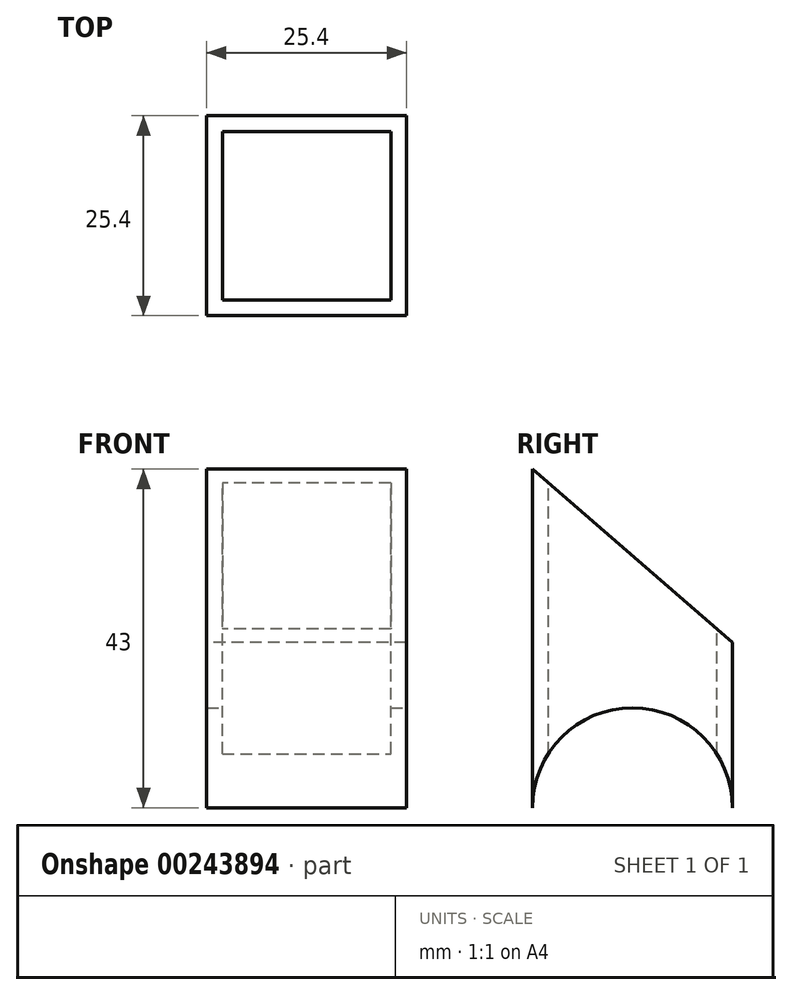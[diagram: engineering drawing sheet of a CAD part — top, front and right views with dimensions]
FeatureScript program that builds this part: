
annotation { "Feature Type Name" : "Feature", "Feature Type Description" : "" }
export const myFeature = defineFeature(function(context is Context, id is Id, definition is map)
    precondition{}
    {
        {
            var Q0;
            Q0=qCreatedBy(makeId("Right.planeOp"),FACE);
            var sketch = newSketch(context, id + "F0", { "sketchPlane" : qUnion([Q0])});
            skLineSegment(sketch, "E0.bottom", {"start": v(-12.7, -21.5) * mm, "end": v(12.7, -21.5) * mm});
            skLineSegment(sketch, "E0.left", {"start": v(-12.7, -21.5) * mm, "end": v(-12.7, 21.5) * mm});
            skLineSegment(sketch, "E0.right", {"start": v(12.7, -21.5) * mm, "end": v(12.7, -0.5) * mm});
            skPoint(sketch, "E0.middle", {"position": v(0, 0) * mm});
            skLineSegment(sketch, "E1", {"start": v(-12.7, 21.5) * mm, "end": v(12.7, -0.5) * mm});
            skSolve(sketch);
        }
        {
            var Q0;
            Q0=makeQuery(id+"F0.imprint","IMPRINT",FACE,{"disambiguationData":[TD([[makeQuery(id+"F0.imprint","IMPRINT",EDGE,{"derivedFrom":sQuery(id+"F0.wireOp",EDGE,"E0.bottom")}),1.0]])]});
            extrude(context, id + "F1", {"entities" : qUnion([Q0]), "endBound" : BoundingType.SYMMETRIC, "depth" : 25.4 * mm});
        }
        {
            var Q0;
            Q0=makeQuery(id+"F1.opExtrude","SWEPT_FACE",FACE,{"disambiguationData":[OSD([sQuery(id+"F0.wireOp",EDGE,"E0.bottom")])]});
            var Q1;
            Q1=makeQuery(id+"F1.opExtrude","SWEPT_FACE",FACE,{"disambiguationData":[OSD([sQuery(id+"F0.wireOp",EDGE,"E1")])]});
            shell(context, id + "F2", {"entities" : qUnion([Q0, Q1]), "thickness" : 2 * mm});
        }
        {
            var Q0;
            Q0=makeQuery(id+"F1.opExtrude","CAP_FACE",FACE,{"disambiguationData":[OSD([sQuery(id+"F0.wireOp",EDGE,"E0.bottom"),sQuery(id+"F0.wireOp",EDGE,"E0.left"),sQuery(id+"F0.wireOp",EDGE,"E0.right"),sQuery(id+"F0.wireOp",EDGE,"E1")])],"isStart":false});
            var sketch = newSketch(context, id + "F3", { "sketchPlane" : qUnion([Q0])});
            skArc(sketch, "E2", {"start": v(12.7, -21.5) * mm, "mid": v(0, -8.8) * mm, "end": v(-12.7, -21.5) * mm});
            skLineSegment(sketch, "E3", {"start": v(-12.7, -21.5) * mm, "end": v(12.7, -21.5) * mm});
            skSolve(sketch);
        }
        {
            var Q0;
            Q0=makeQuery(id+"F3.imprint","IMPRINT",FACE,{"disambiguationData":[TD([[makeQuery(id+"F3.imprint","IMPRINT",EDGE,{"derivedFrom":sQuery(id+"F3.wireOp",EDGE,"E2")}),1.0]])]});
            extrude(context, id + "F4", {"entities" : qUnion([Q0]), "operationType" : NewBodyOperationType.REMOVE, "oppositeDirection" : true, "depth" : 29.08 * mm});
        }
    });
